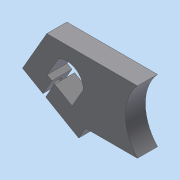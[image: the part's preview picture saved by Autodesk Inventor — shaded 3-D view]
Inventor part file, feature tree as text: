
AUTODESK INVENTOR PART (.ipt)
format: ipt  version: 2017 (Build 210142000, 142)  size: 141,312 bytes
history: native  units: in
note: dims shown in document units (in); Inventor stores cm internally (conversion verified against a paired STEP export)
features: extrude x5, plane x1, sketch x1
ambient origin geometry x8: Origin, YZ Plane, XZ Plane, XY Plane, X Axis, Y Axis, Z Axis, Center Point
bodies: Solid1 (feature_tree)
feature tree (7):
  extrude  "plate"  Depth=0.45in
  extrude  "cut out"  Depth=0.72in
  extrude  "tension holes"  Depth=0.45in
  plane  "Work Plane1"
  sketch  "Sketch2"  dims[d2=2.3228in d3=0.56in d4=0.72in d11=0.45in d20=0.7874in d22=0.5in d23=0.7874in d25=0.75in d45=0.125in d46=0.25in d47=0.0in d48=0.0787in d49=0.5in d50=0.0in d54=0.2in d55=0.0in d56=0.41in d57=1.06in d58=0.45in d59=30.0deg d60=0.1875in d63=-1.2in d67=1.0in d68=0.0in d69=0.816in d83=1.0in d84=0.0in d88=0.25in d89=0.25in d90=0.45in d91=0.313in d92=0.3287in d93=0.36in d94=0.159in]
  extrude  "clamp screw"  Depth=0.5in
  extrude  "clamp nut"  Depth=0.45in
